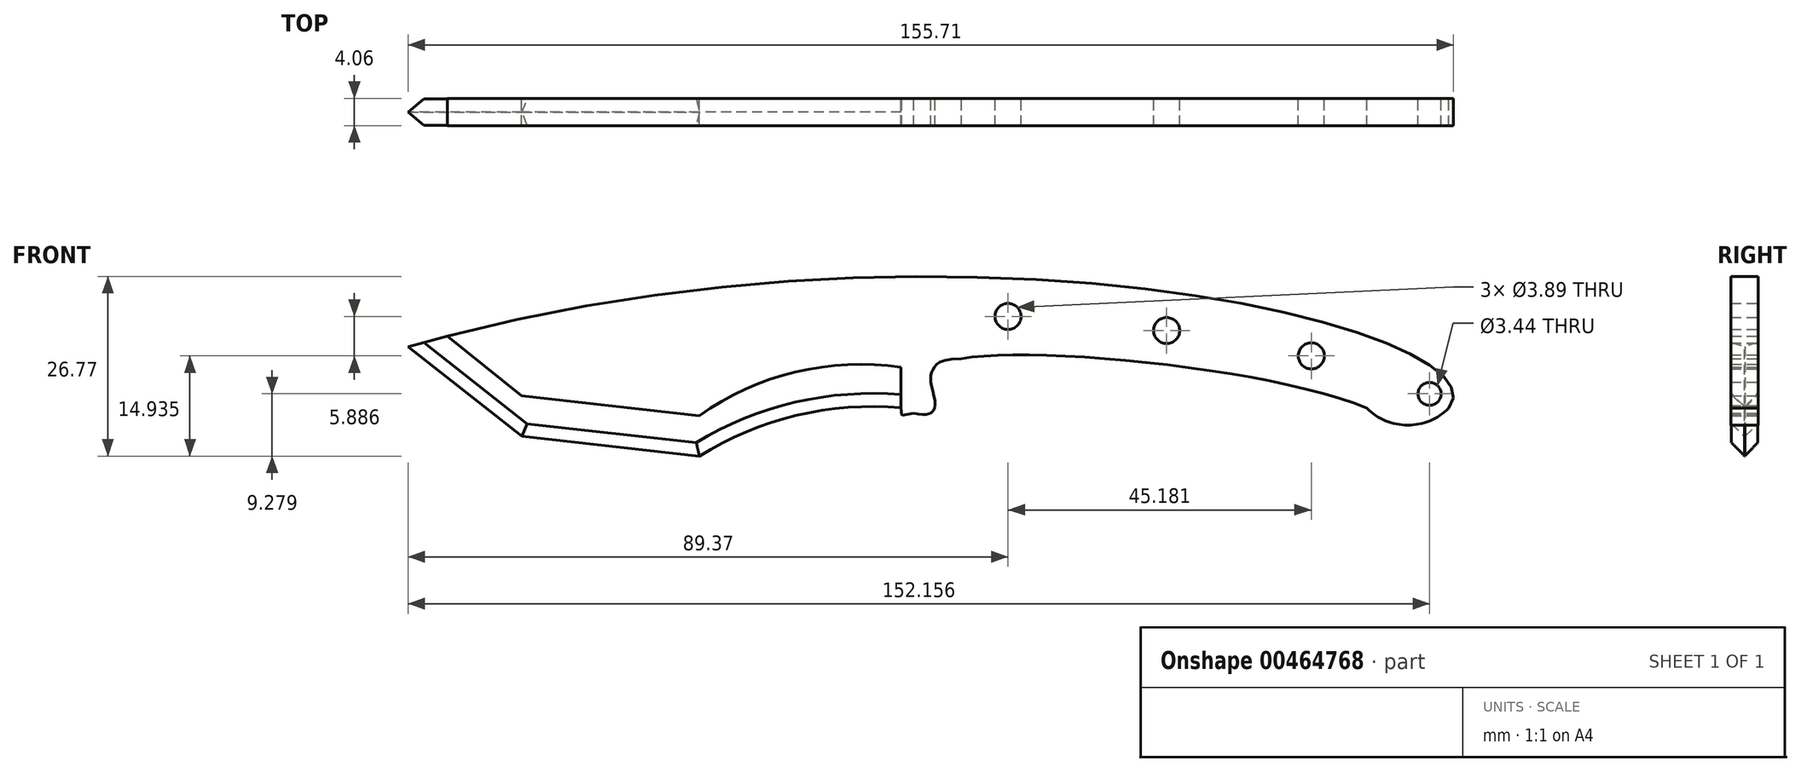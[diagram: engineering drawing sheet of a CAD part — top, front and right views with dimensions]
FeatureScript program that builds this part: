
annotation { "Feature Type Name" : "Feature", "Feature Type Description" : "" }
export const myFeature = defineFeature(function(context is Context, id is Id, definition is map)
    precondition{}
    {
        {
            var Q0;
            Q0=qCreatedBy(makeId("Front.planeOp"),FACE);
            var sketch = newSketch(context, id + "F0", { "sketchPlane" : qUnion([Q0])});
            skFitSpline(sketch, "E0", {"points": [v(-69.47, 27.87) * mm, v(79.71, 17.12) * mm], "startDerivative": vector(238.36, 61.55) * mm, "endDerivative": vector(-26.8, -33.68) * mm});
            skLineSegment(sketch, "E1", {"start": v(-58.32, 12.9) * mm, "end": v(-31.91, 9.96) * mm});
            skFitSpline(sketch, "E2", {"points": [v(0, 16.32) * mm, v(2.43, 16.32) * mm, v(3.2, 17.55) * mm, v(2.55, 21.12) * mm, v(2.88, 22.84) * mm, v(7.11, 24.48) * mm], "startDerivative": vector(18.07, -2.86) * mm, "endDerivative": vector(37.52, 0) * mm});
            skLineSegment(sketch, "E3", {"start": v(0, 16.32) * mm, "end": v(-1.75, 16.04) * mm});
            skLineSegment(sketch, "E4", {"start": v(-1.75, 16.04) * mm, "end": v(-1.87, 17.16) * mm});
            skArc(sketch, "E5", {"start": v(-1.87, 17.16) * mm, "mid": v(-17.48, 16) * mm, "end": v(-31.91, 9.96) * mm});
            skLineSegment(sketch, "E6", {"start": v(-58.42, 18.95) * mm, "end": v(-31.91, 16) * mm});
            skLineSegment(sketch, "E7", {"start": v(-1.87, 17.16) * mm, "end": v(-1.87, 23.2) * mm});
            skArc(sketch, "E8", {"start": v(-1.87, 23.2) * mm, "mid": v(-17.59, 22.5) * mm, "end": v(-31.91, 16) * mm});
            skLineSegment(sketch, "E9", {"start": v(-58.32, 12.9) * mm, "end": v(-75.3, 26.27) * mm});
            skLineSegment(sketch, "E10", {"start": v(-58.42, 18.95) * mm, "end": v(-58.32, 12.9) * mm});
            skLineSegment(sketch, "E11", {"start": v(-31.91, 16) * mm, "end": v(-31.91, 9.96) * mm});
            skPoint(sketch, "E12", {"position": v(37.7, 34.47) * mm});
            skFitSpline(sketch, "E13", {"points": [v(7.11, 24.48) * mm, v(67.5, 17.12) * mm], "startDerivative": vector(32.5, 6.07) * mm, "endDerivative": vector(41.2, -17.48) * mm});
            skPoint(sketch, "E14", {"position": v(37.7, 23.57) * mm});
            skArc(sketch, "E15", {"start": v(67.5, 17.12) * mm, "mid": v(73.61, 14.57) * mm, "end": v(79.71, 17.12) * mm});
            skPoint(sketch, "E16", {"position": v(-9.81, 36.49) * mm});
            skCircle(sketch, "E17", {"center": v(76.86, 19.24) * mm, "radius": 1.72 * mm});
            skCircle(sketch, "E18", {"center": v(14.07, 30.78) * mm, "radius": 1.94 * mm});
            skCircle(sketch, "E19", {"center": v(37.7, 28.68) * mm, "radius": 1.94 * mm});
            skCircle(sketch, "E20", {"center": v(59.25, 24.9) * mm, "radius": 1.94 * mm});
            skPoint(sketch, "E21", {"position": v(14.07, 36.48) * mm});
            skPoint(sketch, "E22", {"position": v(41.42, 33.95) * mm});
            skPoint(sketch, "E23", {"position": v(59.25, 30.4) * mm});
            skLineSegment(sketch, "E24", {"start": v(-58.42, 18.95) * mm, "end": v(-69.47, 27.87) * mm});
            skLineSegment(sketch, "E25", {"start": v(-69.47, 27.87) * mm, "end": v(-75.3, 26.27) * mm});
            skSolve(sketch);
        }
        {
            var Q0;
            Q0=makeQuery(id+"F0.imprint","IMPRINT",FACE,{"disambiguationData":[TD([[makeQuery(id+"F0.imprint","IMPRINT",EDGE,{"derivedFrom":sQuery(id+"F0.wireOp",EDGE,"E2")}),1.0]])]});
            extrude(context, id + "F1", {"entities" : qUnion([Q0]), "endBound" : BoundingType.SYMMETRIC, "depth" : 4.06 * mm});
        }
        {
            var Q0;
            Q0=makeQuery(id+"F0.imprint","IMPRINT",FACE,{"disambiguationData":[TD([[makeQuery(id+"F0.imprint","IMPRINT",EDGE,{"derivedFrom":sQuery(id+"F0.wireOp",EDGE,"E9")}),-1.0]])]});
            var Q1;
            Q1=makeQuery(id+"F0.imprint","IMPRINT",FACE,{"disambiguationData":[TD([[makeQuery(id+"F0.imprint","IMPRINT",EDGE,{"derivedFrom":sQuery(id+"F0.wireOp",EDGE,"E1")}),1.0]])]});
            var Q2;
            Q2=makeQuery(id+"F0.imprint","IMPRINT",FACE,{"disambiguationData":[TD([[makeQuery(id+"F0.imprint","IMPRINT",EDGE,{"derivedFrom":sQuery(id+"F0.wireOp",EDGE,"E5")}),-1.0]])]});
            extrude(context, id + "F2", {"entities" : qUnion([Q0, Q1, Q2]), "endBound" : BoundingType.SYMMETRIC, "depth" : 3.94 * mm});
        }
        {
            var Q0;
            Q0=makeQuery(id+"F2.opExtrude","CAP_EDGE",EDGE,{"disambiguationData":[OSD([sQuery(id+"F0.wireOp",EDGE,"E5")])],"isStart":false});
            var Q1;
            Q1=makeQuery(id+"F2.opExtrude","CAP_EDGE",EDGE,{"disambiguationData":[OSD([sQuery(id+"F0.wireOp",EDGE,"E5")])],"isStart":true});
            var Q2;
            Q2=makeQuery(id+"F2.opExtrude","CAP_EDGE",EDGE,{"disambiguationData":[OSD([sQuery(id+"F0.wireOp",EDGE,"E1")])],"isStart":false});
            var Q3;
            Q3=makeQuery(id+"F2.opExtrude","CAP_EDGE",EDGE,{"disambiguationData":[OSD([sQuery(id+"F0.wireOp",EDGE,"E1")])],"isStart":true});
            var Q4;
            Q4=makeQuery(id+"F2.opExtrude","CAP_EDGE",EDGE,{"disambiguationData":[OSD([sQuery(id+"F0.wireOp",EDGE,"E9")])],"isStart":false});
            var Q5;
            Q5=makeQuery(id+"F2.opExtrude","CAP_EDGE",EDGE,{"disambiguationData":[OSD([sQuery(id+"F0.wireOp",EDGE,"E9")])],"isStart":true});
            chamfer(context, id + "F3", {"entities" : qUnion([Q0, Q1, Q2, Q3, Q4, Q5]), "width" : 1.96 * mm, "tangentPropagation" : true});
        }
    });
